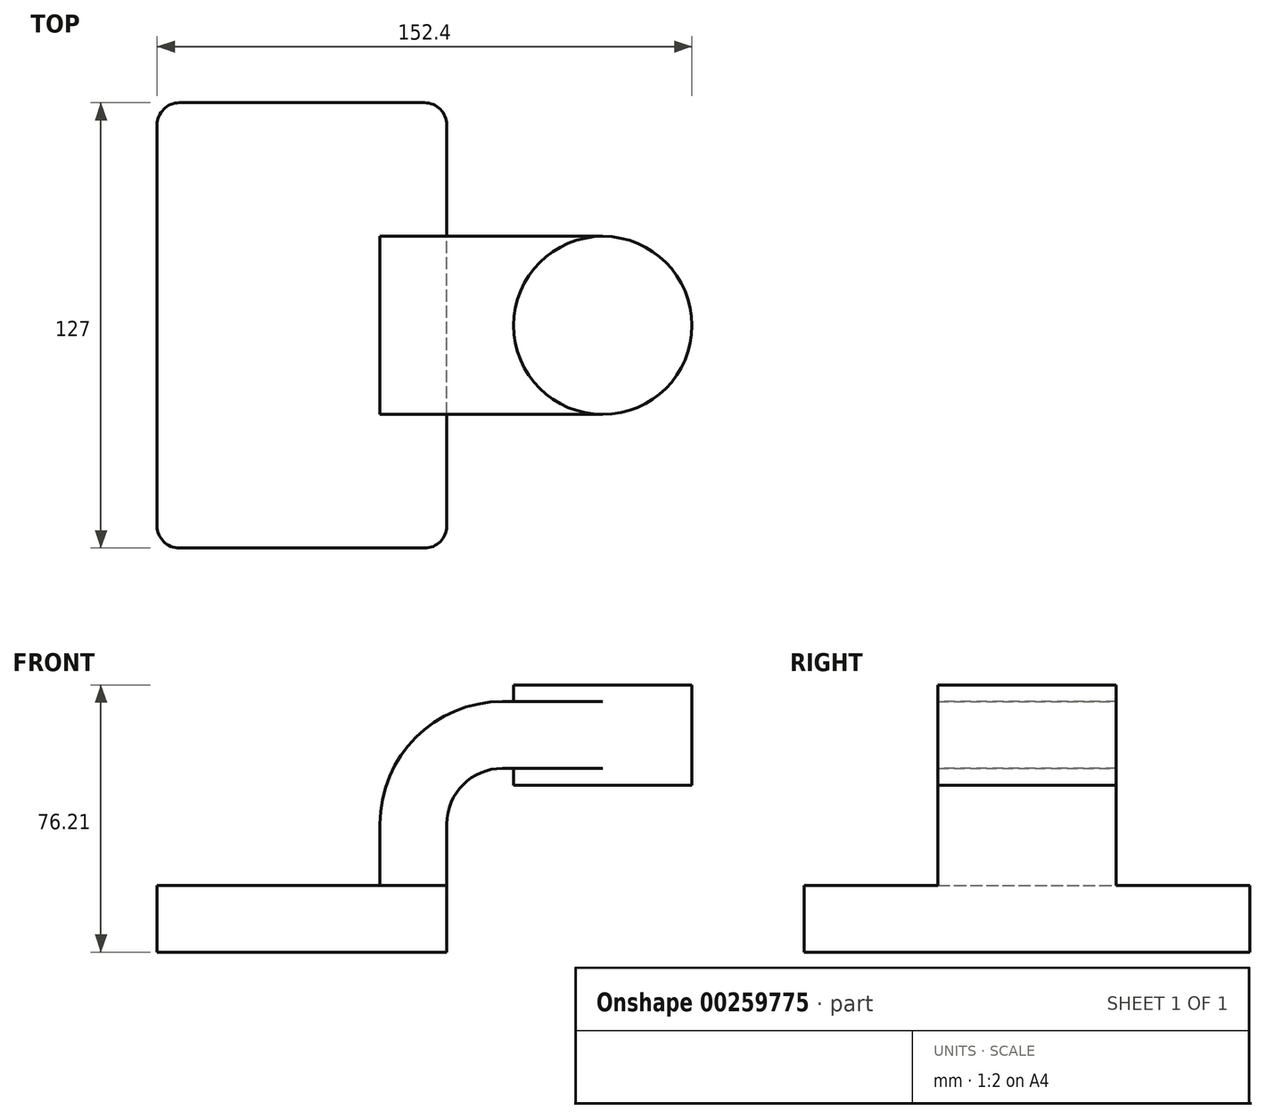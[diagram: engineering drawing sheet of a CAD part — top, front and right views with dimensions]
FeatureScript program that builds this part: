
annotation { "Feature Type Name" : "Feature", "Feature Type Description" : "" }
export const myFeature = defineFeature(function(context is Context, id is Id, definition is map)
    precondition{}
    {
        {
            var Q0;
            Q0=qCreatedBy(makeId("Front.planeOp"),FACE);
            var sketch = newSketch(context, id + "F0", { "sketchPlane" : qUnion([Q0])});
            skLineSegment(sketch, "E0.bottom", {"start": v(41.27, 9.53) * mm, "end": v(-41.27, 9.53) * mm});
            skLineSegment(sketch, "E0.top", {"start": v(41.28, -9.52) * mm, "end": v(-41.27, -9.52) * mm});
            skLineSegment(sketch, "E0.left", {"start": v(41.28, 9.53) * mm, "end": v(41.28, -9.52) * mm});
            skLineSegment(sketch, "E0.right", {"start": v(-41.27, 9.53) * mm, "end": v(-41.27, -9.52) * mm});
            skPoint(sketch, "E0.middle", {"position": v(0, 0) * mm});
            skLineSegment(sketch, "E1.bottom", {"start": v(111.12, 38.1) * mm, "end": v(60.32, 38.1) * mm});
            skLineSegment(sketch, "E1.top", {"start": v(111.12, 66.68) * mm, "end": v(60.32, 66.68) * mm});
            skLineSegment(sketch, "E1.left", {"start": v(111.12, 38.1) * mm, "end": v(111.12, 66.68) * mm});
            skLineSegment(sketch, "E1.right", {"start": v(60.32, 38.1) * mm, "end": v(60.32, 66.68) * mm});
            skPoint(sketch, "E1.middle", {"position": v(85.72, 52.39) * mm});
            skLineSegment(sketch, "E2", {"start": v(41.28, 9.53) * mm, "end": v(41.28, 27) * mm});
            skPoint(sketch, "E3.endSnap0", {"position": v(60.32, 52.39) * mm});
            skArc(sketch, "E4", {"start": v(41.28, 27) * mm, "mid": v(45.92, 38.23) * mm, "end": v(57.15, 42.88) * mm});
            skLineSegment(sketch, "E5", {"start": v(57.15, 42.88) * mm, "end": v(85.72, 42.88) * mm});
            skLineSegment(sketch, "E6.0", {"start": v(57.15, 61.93) * mm, "end": v(85.72, 61.93) * mm});
            skArc(sketch, "E6.1", {"start": v(22.23, 27) * mm, "mid": v(32.45, 51.7) * mm, "end": v(57.15, 61.93) * mm});
            skLineSegment(sketch, "E6.2", {"start": v(22.23, 9.53) * mm, "end": v(22.23, 27) * mm});
            skLineSegment(sketch, "E7", {"start": v(85.72, 66.68) * mm, "end": v(85.72, 38.1) * mm});
            skFitSpline(sketch, "E8", {"points": [v(-41.27, 9.52) * mm, v(57.15, 61.93) * mm], "startDerivative": vector(0.07, 102.93) * mm, "endDerivative": vector(149.96, -5.25) * mm});
            skSolve(sketch);
        }
        {
            var Q0;
            Q0=makeQuery(id+"F0.imprint","IMPRINT",FACE,{"disambiguationData":[TD([[makeQuery(id+"F0.imprint","IMPRINT",EDGE,{"derivedFrom":sQuery(id+"F0.wireOp",EDGE,"E0.top")}),-1.0]])]});
            extrude(context, id + "F1", {"entities" : qUnion([Q0]), "endBound" : BoundingType.SYMMETRIC, "depth" : 127 * mm});
        }
        {
            var Q0;
            {var subQ1=sQuery(id+"F0.wireOp",EDGE,"E2");Q0=makeQuery(id+"F0.imprint","IMPRINT",FACE,{"disambiguationData":[TD([[makeQuery(id+"F0.imprint","IMPRINT",EDGE,{"derivedFrom":subQ1}),1.0]])]});}
            extrude(context, id + "F2", {"entities" : qUnion([Q0]), "operationType" : NewBodyOperationType.ADD, "endBound" : BoundingType.SYMMETRIC, "depth" : 50.8 * mm});
        }
        {
            var Q0;
            Q0=makeQuery(id+"F0.imprint","IMPRINT",FACE,{"disambiguationData":[TD([[makeQuery(id+"F0.imprint","IMPRINT",EDGE,{"derivedFrom":sQuery(id+"F0.wireOp",EDGE,"E6.1")}),1.0]])]});
            extrude(context, id + "F3", {"entities" : qUnion([Q0]), "operationType" : NewBodyOperationType.ADD, "endBound" : BoundingType.SYMMETRIC, "depth" : 15.88 * mm});
        }
        {
            var Q0;
            {var subQ0=sQuery(id+"F0.wireOp",EDGE,"E5");var subQ1=sQuery(id+"F0.wireOp",EDGE,"E1.right");var subQ2=makeQuery(id+"F0.imprint","INTERSECT",VERTEX,{"derivedFrom":[subQ1,subQ0]});Q0=makeQuery(id+"F0.imprint","IMPRINT",FACE,{"disambiguationData":[TD([[makeQuery(id+"F0.imprint","IMPRINT",EDGE,{"disambiguationData":[TD([[subQ2,-1.0]])],"derivedFrom":subQ1}),-1.0]])]});}
            extrude(context, id + "F4", {"entities" : qUnion([Q0]), "operationType" : NewBodyOperationType.ADD, "endBound" : BoundingType.SYMMETRIC, "depth" : 50.8 * mm});
        }
        {
            var Q0;
            {var subQ0=sQuery(id+"F0.wireOp",EDGE,"E1.left");Q0=makeQuery(id+"F0.imprint","IMPRINT",FACE,{"disambiguationData":[TD([[makeQuery(id+"F0.imprint","IMPRINT",EDGE,{"derivedFrom":subQ0}),1.0]])]});}
            var Q1;
            Q1=sQuery(id+"F0.wireOp",EDGE,"E7");
            revolve(context, id + "F5", {"operationType" : NewBodyOperationType.ADD, "entities" : qUnion([Q0]), "axis" : qUnion([Q1]), "revolveType" : RevolveType.FULL});
        }
        {
            var Q0;
            Q0=makeQuery(id+"F1.opExtrude","CAP_EDGE",EDGE,{"disambiguationData":[OSD([sQuery(id+"F0.wireOp",EDGE,"E0.left")])],"isStart":true});
            var Q1;
            Q1=makeQuery(id+"F1.opExtrude","CAP_EDGE",EDGE,{"disambiguationData":[OSD([sQuery(id+"F0.wireOp",EDGE,"E0.right")])],"isStart":true});
            var Q2;
            Q2=makeQuery(id+"F1.opExtrude","CAP_EDGE",EDGE,{"disambiguationData":[OSD([sQuery(id+"F0.wireOp",EDGE,"E0.right")])],"isStart":false});
            fillet(context, id + "F6", {"entities" : qUnion([Q0, Q1, Q2]), "radius" : 6.35 * mm, "tangentPropagation" : true, "allowEdgeOverflow" : false});
        }
        {
            var Q0;
            Q0=makeQuery(id+"F1.opExtrude","CAP_EDGE",EDGE,{"disambiguationData":[OSD([sQuery(id+"F0.wireOp",EDGE,"E0.left")])],"isStart":false});
            fillet(context, id + "F7", {"entities" : qUnion([Q0]), "radius" : 6.35 * mm, "tangentPropagation" : true, "allowEdgeOverflow" : false});
        }
    });
